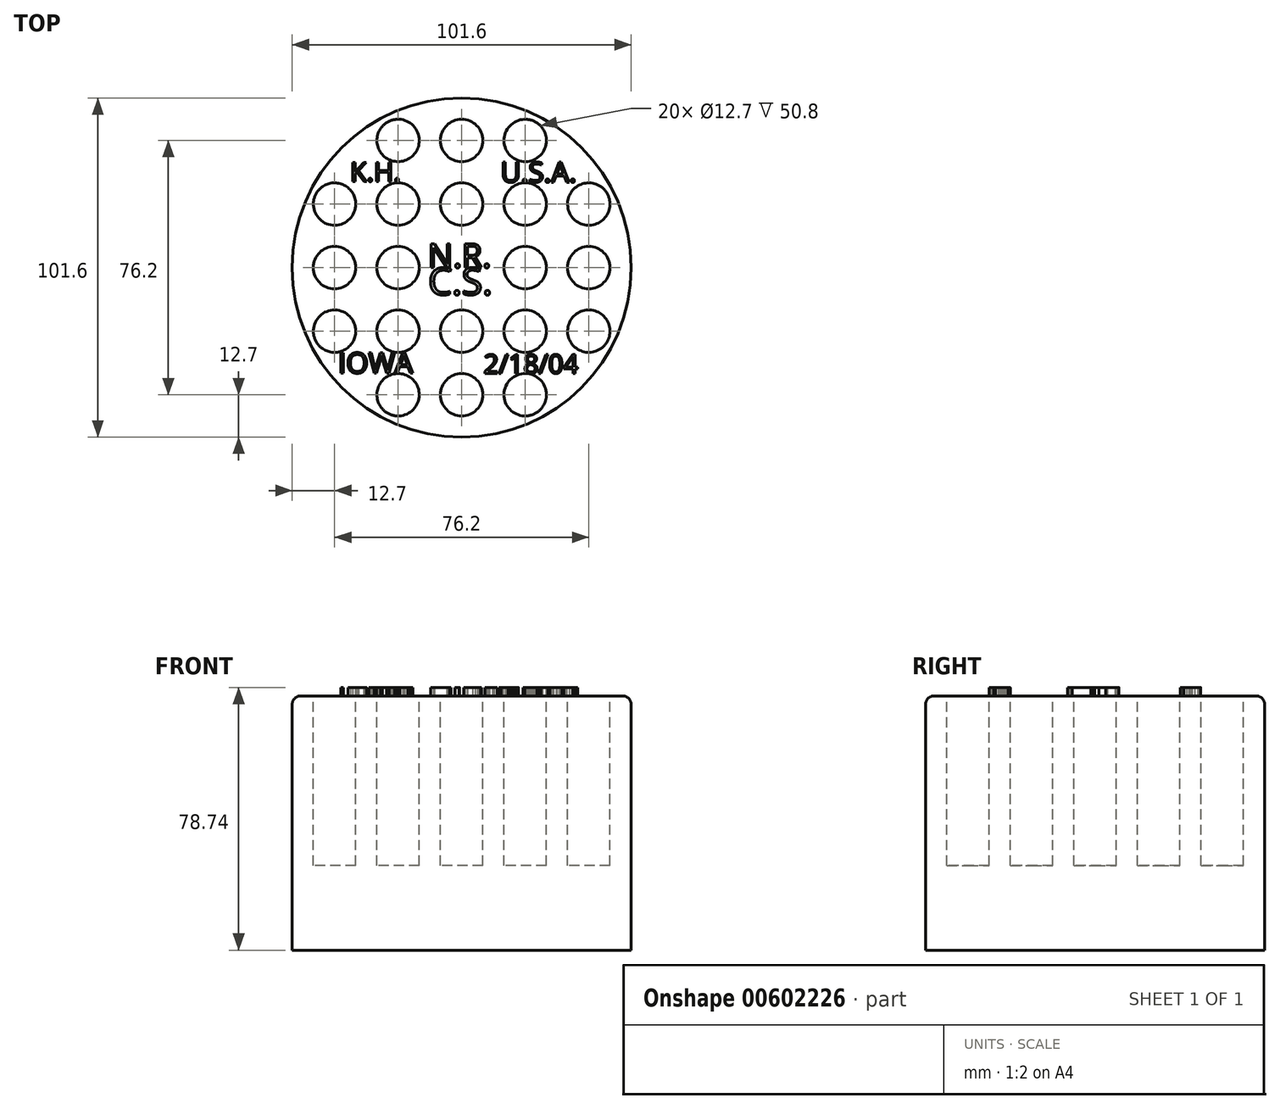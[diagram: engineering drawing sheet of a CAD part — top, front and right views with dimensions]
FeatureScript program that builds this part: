
annotation { "Feature Type Name" : "Feature", "Feature Type Description" : "" }
export const myFeature = defineFeature(function(context is Context, id is Id, definition is map)
    precondition{}
    {
        {
            var Q0;
            Q0=qCreatedBy(makeId("Top.planeOp"),FACE);
            var sketch = newSketch(context, id + "F0", { "sketchPlane" : qUnion([Q0])});
            skCircle(sketch, "E0", {"center": v(0, 0) * mm, "radius": 50.8 * mm});
            skSolve(sketch);
        }
        {
            var Q0;
            Q0=makeQuery(id+"F0.imprint","IMPRINT",FACE,{"disambiguationData":[TD([[makeQuery(id+"F0.imprint","IMPRINT",EDGE,{"derivedFrom":sQuery(id+"F0.wireOp",EDGE,"E0")}),1.0]])]});
            extrude(context, id + "F1", {"entities" : qUnion([Q0]), "depth" : 50.8 * mm, "offsetDistance" : 25.4 * mm, "hasSecondDirection" : true, "secondDirectionOppositeDirection" : true, "secondDirectionDepth" : 25.4 * mm});
        }
        {
            var Q0;
            Q0=makeQuery(id+"F1.opExtrude","CAP_FACE",FACE,{"disambiguationData":[OSD([sQuery(id+"F0.wireOp",EDGE,"E0")])],"isStart":false});
            var sketch = newSketch(context, id + "F2", { "sketchPlane" : qUnion([Q0])});
            skCircle(sketch, "E1", {"center": v(-19.05, 0) * mm, "radius": 6.35 * mm});
            skCircle(sketch, "E2", {"center": v(19.05, 0) * mm, "radius": 6.35 * mm});
            skCircle(sketch, "E3", {"center": v(38.1, 0) * mm, "radius": 6.35 * mm});
            skCircle(sketch, "E4", {"center": v(-38.1, 0) * mm, "radius": 6.35 * mm});
            skCircle(sketch, "E5", {"center": v(0, 19.05) * mm, "radius": 6.35 * mm});
            skCircle(sketch, "E6", {"center": v(0, 38.1) * mm, "radius": 6.35 * mm});
            skCircle(sketch, "E7", {"center": v(0, -19.05) * mm, "radius": 6.35 * mm});
            skCircle(sketch, "E8", {"center": v(0, -38.1) * mm, "radius": 6.35 * mm});
            skCircle(sketch, "E9", {"center": v(19.05, 19.05) * mm, "radius": 6.35 * mm});
            skCircle(sketch, "E10", {"center": v(38.1, 19.05) * mm, "radius": 6.35 * mm});
            skCircle(sketch, "E11", {"center": v(19.05, 38.1) * mm, "radius": 6.35 * mm});
            skCircle(sketch, "E12", {"center": v(-19.05, 19.05) * mm, "radius": 6.35 * mm});
            skCircle(sketch, "E13", {"center": v(-38.1, 19.05) * mm, "radius": 6.35 * mm});
            skCircle(sketch, "E14", {"center": v(-19.05, 38.1) * mm, "radius": 6.35 * mm});
            skCircle(sketch, "E15", {"center": v(19.05, -19.05) * mm, "radius": 6.35 * mm});
            skCircle(sketch, "E16", {"center": v(38.1, -19.05) * mm, "radius": 6.35 * mm});
            skCircle(sketch, "E17", {"center": v(19.05, -38.1) * mm, "radius": 6.35 * mm});
            skCircle(sketch, "E18", {"center": v(-19.05, -38.1) * mm, "radius": 6.35 * mm});
            skCircle(sketch, "E19", {"center": v(-19.05, -19.05) * mm, "radius": 6.35 * mm});
            skCircle(sketch, "E20", {"center": v(-38.1, -19.05) * mm, "radius": 6.35 * mm});
            skSolve(sketch);
        }
        {
            var Q0;
            Q0=makeQuery(id+"F2.imprint","IMPRINT",FACE,{"disambiguationData":[TD([[makeQuery(id+"F2.imprint","IMPRINT",EDGE,{"derivedFrom":sQuery(id+"F2.wireOp",EDGE,"E10")}),1.0]])]});
            var Q1;
            Q1=makeQuery(id+"F2.imprint","IMPRINT",FACE,{"disambiguationData":[TD([[makeQuery(id+"F2.imprint","IMPRINT",EDGE,{"derivedFrom":sQuery(id+"F2.wireOp",EDGE,"E11")}),1.0]])]});
            var Q2;
            Q2=makeQuery(id+"F2.imprint","IMPRINT",FACE,{"disambiguationData":[TD([[makeQuery(id+"F2.imprint","IMPRINT",EDGE,{"derivedFrom":sQuery(id+"F2.wireOp",EDGE,"E9")}),1.0]])]});
            var Q3;
            Q3=makeQuery(id+"F2.imprint","IMPRINT",FACE,{"disambiguationData":[TD([[makeQuery(id+"F2.imprint","IMPRINT",EDGE,{"derivedFrom":sQuery(id+"F2.wireOp",EDGE,"E2")}),1.0]])]});
            var Q4;
            Q4=makeQuery(id+"F2.imprint","IMPRINT",FACE,{"disambiguationData":[TD([[makeQuery(id+"F2.imprint","IMPRINT",EDGE,{"derivedFrom":sQuery(id+"F2.wireOp",EDGE,"E5")}),1.0]])]});
            var Q5;
            Q5=makeQuery(id+"F2.imprint","IMPRINT",FACE,{"disambiguationData":[TD([[makeQuery(id+"F2.imprint","IMPRINT",EDGE,{"derivedFrom":sQuery(id+"F2.wireOp",EDGE,"E6")}),1.0]])]});
            var Q6;
            Q6=makeQuery(id+"F2.imprint","IMPRINT",FACE,{"disambiguationData":[TD([[makeQuery(id+"F2.imprint","IMPRINT",EDGE,{"derivedFrom":sQuery(id+"F2.wireOp",EDGE,"E14")}),1.0]])]});
            var Q7;
            Q7=makeQuery(id+"F2.imprint","IMPRINT",FACE,{"disambiguationData":[TD([[makeQuery(id+"F2.imprint","IMPRINT",EDGE,{"derivedFrom":sQuery(id+"F2.wireOp",EDGE,"E12")}),1.0]])]});
            var Q8;
            Q8=makeQuery(id+"F2.imprint","IMPRINT",FACE,{"disambiguationData":[TD([[makeQuery(id+"F2.imprint","IMPRINT",EDGE,{"derivedFrom":sQuery(id+"F2.wireOp",EDGE,"E13")}),1.0]])]});
            var Q9;
            Q9=makeQuery(id+"F2.imprint","IMPRINT",FACE,{"disambiguationData":[TD([[makeQuery(id+"F2.imprint","IMPRINT",EDGE,{"derivedFrom":sQuery(id+"F2.wireOp",EDGE,"E4")}),1.0]])]});
            var Q10;
            Q10=makeQuery(id+"F2.imprint","IMPRINT",FACE,{"disambiguationData":[TD([[makeQuery(id+"F2.imprint","IMPRINT",EDGE,{"derivedFrom":sQuery(id+"F2.wireOp",EDGE,"E1")}),1.0]])]});
            var Q11;
            Q11=makeQuery(id+"F2.imprint","IMPRINT",FACE,{"disambiguationData":[TD([[makeQuery(id+"F2.imprint","IMPRINT",EDGE,{"derivedFrom":sQuery(id+"F2.wireOp",EDGE,"Gjw0qyJ1-Gvtr-FgdP-XmZ9-gWnnEZj1rsvU")}),1.0]])]});
            var Q12;
            Q12=makeQuery(id+"F2.imprint","IMPRINT",FACE,{"disambiguationData":[TD([[makeQuery(id+"F2.imprint","IMPRINT",EDGE,{"derivedFrom":sQuery(id+"F2.wireOp",EDGE,"E7")}),1.0]])]});
            var Q13;
            Q13=makeQuery(id+"F2.imprint","IMPRINT",FACE,{"disambiguationData":[TD([[makeQuery(id+"F2.imprint","IMPRINT",EDGE,{"derivedFrom":sQuery(id+"F2.wireOp",EDGE,"E19")}),1.0]])]});
            var Q14;
            Q14=makeQuery(id+"F2.imprint","IMPRINT",FACE,{"disambiguationData":[TD([[makeQuery(id+"F2.imprint","IMPRINT",EDGE,{"derivedFrom":sQuery(id+"F2.wireOp",EDGE,"E20")}),1.0]])]});
            var Q15;
            Q15=makeQuery(id+"F2.imprint","IMPRINT",FACE,{"disambiguationData":[TD([[makeQuery(id+"F2.imprint","IMPRINT",EDGE,{"derivedFrom":sQuery(id+"F2.wireOp",EDGE,"E15")}),1.0]])]});
            var Q16;
            Q16=makeQuery(id+"F2.imprint","IMPRINT",FACE,{"disambiguationData":[TD([[makeQuery(id+"F2.imprint","IMPRINT",EDGE,{"derivedFrom":sQuery(id+"F2.wireOp",EDGE,"E17")}),1.0]])]});
            var Q17;
            Q17=makeQuery(id+"F2.imprint","IMPRINT",FACE,{"disambiguationData":[TD([[makeQuery(id+"F2.imprint","IMPRINT",EDGE,{"derivedFrom":sQuery(id+"F2.wireOp",EDGE,"E8")}),1.0]])]});
            var Q18;
            Q18=makeQuery(id+"F2.imprint","IMPRINT",FACE,{"disambiguationData":[TD([[makeQuery(id+"F2.imprint","IMPRINT",EDGE,{"derivedFrom":sQuery(id+"F2.wireOp",EDGE,"E18")}),1.0]])]});
            var Q19;
            Q19=makeQuery(id+"F2.imprint","IMPRINT",FACE,{"disambiguationData":[TD([[makeQuery(id+"F2.imprint","IMPRINT",EDGE,{"derivedFrom":sQuery(id+"F2.wireOp",EDGE,"E16")}),1.0]])]});
            var Q20;
            Q20=makeQuery(id+"F2.imprint","IMPRINT",FACE,{"disambiguationData":[TD([[makeQuery(id+"F2.imprint","IMPRINT",EDGE,{"derivedFrom":sQuery(id+"F2.wireOp",EDGE,"E3")}),1.0]])]});
            extrude(context, id + "F3", {"entities" : qUnion([Q0, Q1, Q2, Q3, Q4, Q5, Q6, Q7, Q8, Q9, Q10, Q11, Q12, Q13, Q14, Q15, Q16, Q17, Q18, Q19, Q20]), "operationType" : NewBodyOperationType.REMOVE, "oppositeDirection" : true, "depth" : 50.8 * mm, "offsetDistance" : 25.4 * mm});
        }
        {
            var Q0;
            Q0=makeQuery(id+"F1.opExtrude","CAP_FACE",FACE,{"disambiguationData":[OSD([sQuery(id+"F0.wireOp",EDGE,"E0")])],"isStart":false});
            var sketch = newSketch(context, id + "F4", { "sketchPlane" : qUnion([Q0])});
            skText(sketch, "E21", { "text": "N.", "fontName": "OpenSans-Regular.ttf"});
            skText(sketch, "E22", { "text": "R.", "fontName": "OpenSans-Regular.ttf"});
            skText(sketch, "E23", { "text": "C.", "fontName": "OpenSans-Regular.ttf"});
            skText(sketch, "E24", { "text": "S.\n", "fontName": "OpenSans-Regular.ttf"});
            const initialGuessF4  = {"E21": [-0.0101, 0, 1, 0, 0.0072], "E22": [0, 0, 1, 0, 0.0072], "E23": [-0.01003, -0.00814, 1, 0, 0.00814], "E24": [0, -0.00813, 1, 0, 0.00813]};
            skSetInitialGuess(sketch, initialGuessF4);
            skSolve(sketch);
        }
        {
            var Q0;
            Q0 = qSketchRegion(id + "F4", true);
            extrude(context, id + "F5", {"entities" : qUnion([Q0]), "operationType" : NewBodyOperationType.ADD, "depth" : 2.54 * mm, "offsetDistance" : 25.4 * mm});
        }
        {
            var Q0;
            {var subQ0=sQuery(id+"F0.wireOp",EDGE,"E0");Q0=makeQuery(id+"F5.boolean.opBoolean","SPLIT",FACE,{"disambiguationData":[TD([makeQuery(id+"F1.opExtrude","SWEPT_FACE",FACE,{"disambiguationData":[OSD([subQ0])]})])],"derivedFrom":makeQuery(id+"F1.opExtrude","CAP_FACE",FACE,{"disambiguationData":[OSD([subQ0])],"isStart":false})});}
            var sketch = newSketch(context, id + "F6", { "sketchPlane" : qUnion([Q0])});
            skText(sketch, "E25", { "text": "K.H.", "fontName": "OpenSans-Regular.ttf"});
            const initialGuessF6  = {"E25": [-0.0334, 0.02583, 1, 0, 0.00578]};
            skSetInitialGuess(sketch, initialGuessF6);
            skSolve(sketch);
        }
        {
            var Q0;
            Q0 = qSketchRegion(id + "F6", true);
            extrude(context, id + "F7", {"entities" : qUnion([Q0]), "operationType" : NewBodyOperationType.ADD, "depth" : 2.54 * mm, "offsetDistance" : 25.4 * mm});
        }
        {
            var Q0;
            {var subQ0=sQuery(id+"F0.wireOp",EDGE,"E0");Q0=makeQuery(id+"F5.boolean.opBoolean","SPLIT",FACE,{"disambiguationData":[TD([makeQuery(id+"F1.opExtrude","SWEPT_FACE",FACE,{"disambiguationData":[OSD([subQ0])]})])],"derivedFrom":makeQuery(id+"F1.opExtrude","CAP_FACE",FACE,{"disambiguationData":[OSD([subQ0])],"isStart":false})});}
            var sketch = newSketch(context, id + "F8", { "sketchPlane" : qUnion([Q0])});
            skText(sketch, "E26", { "text": "U.S.A.", "fontName": "OpenSans-Regular.ttf"});
            const initialGuessF8  = {"E26": [0.01167, 0.02559, 1, 0, 0.00605]};
            skSetInitialGuess(sketch, initialGuessF8);
            skSolve(sketch);
        }
        {
            var Q0;
            Q0 = qSketchRegion(id + "F8", true);
            extrude(context, id + "F9", {"entities" : qUnion([Q0]), "operationType" : NewBodyOperationType.ADD, "depth" : 2.54 * mm, "offsetDistance" : 25.4 * mm});
        }
        {
            var Q0;
            {var subQ45=sQuery(id+"F0.wireOp",EDGE,"E0");var subQ46=makeQuery(id+"F1.opExtrude","SWEPT_FACE",FACE,{"disambiguationData":[OSD([subQ45])]});Q0=makeQuery(id+"F9.boolean.opBoolean","SPLIT",FACE,{"disambiguationData":[TD([subQ46])],"derivedFrom":makeQuery(id+"F5.boolean.opBoolean","SPLIT",FACE,{"disambiguationData":[TD([subQ46])],"derivedFrom":makeQuery(id+"F1.opExtrude","CAP_FACE",FACE,{"disambiguationData":[OSD([subQ45])],"isStart":false})})});}
            var sketch = newSketch(context, id + "F10", { "sketchPlane" : qUnion([Q0])});
            skText(sketch, "E27", { "text": "IOWA", "fontName": "OpenSans-Regular.ttf"});
            const initialGuessF10  = {"E27": [-0.037, -0.03163, 1, 0, 0.00616]};
            skSetInitialGuess(sketch, initialGuessF10);
            skSolve(sketch);
        }
        {
            var Q0;
            Q0 = qSketchRegion(id + "F10", true);
            extrude(context, id + "F11", {"entities" : qUnion([Q0]), "operationType" : NewBodyOperationType.ADD, "depth" : 2.54 * mm, "offsetDistance" : 25.4 * mm});
        }
        {
            var Q0;
            {var subQ82=sQuery(id+"F0.wireOp",EDGE,"E0");var subQ83=makeQuery(id+"F1.opExtrude","SWEPT_FACE",FACE,{"disambiguationData":[OSD([subQ82])]});Q0=makeQuery(id+"F11.boolean.opBoolean","SPLIT",FACE,{"disambiguationData":[TD([subQ83])],"derivedFrom":makeQuery(id+"F9.boolean.opBoolean","SPLIT",FACE,{"disambiguationData":[TD([subQ83])],"derivedFrom":makeQuery(id+"F5.boolean.opBoolean","SPLIT",FACE,{"disambiguationData":[TD([subQ83])],"derivedFrom":makeQuery(id+"F1.opExtrude","CAP_FACE",FACE,{"disambiguationData":[OSD([subQ82])],"isStart":false})})})});}
            var sketch = newSketch(context, id + "F12", { "sketchPlane" : qUnion([Q0])});
            skText(sketch, "E28", { "text": "2/18/04", "fontName": "OpenSans-Regular.ttf"});
            const initialGuessF12  = {"E28": [0.00663, -0.0317, 1, 0, 0.00568]};
            skSetInitialGuess(sketch, initialGuessF12);
            skSolve(sketch);
        }
        {
            var Q0;
            Q0 = qSketchRegion(id + "F12", true);
            extrude(context, id + "F13", {"entities" : qUnion([Q0]), "operationType" : NewBodyOperationType.ADD, "depth" : 2.54 * mm, "offsetDistance" : 25.4 * mm});
        }
        {
            var Q0;
            Q0=makeQuery(id+"F1.opExtrude","CAP_EDGE",EDGE,{"disambiguationData":[OSD([sQuery(id+"F0.wireOp",EDGE,"E0")])],"isStart":false});
            fillet(context, id + "F14", {"entities" : qUnion([Q0]), "radius" : 2.54 * mm, "tangentPropagation" : true, "allowEdgeOverflow" : false});
        }
    });
